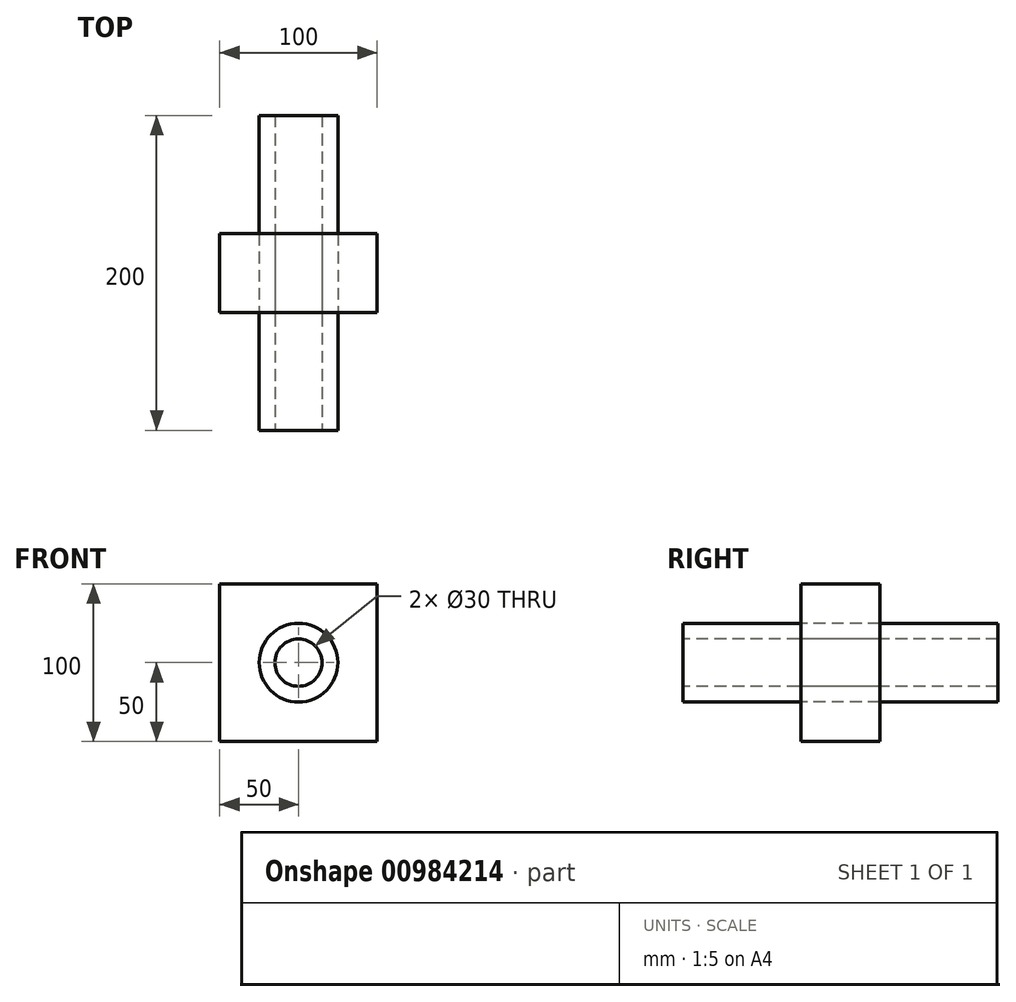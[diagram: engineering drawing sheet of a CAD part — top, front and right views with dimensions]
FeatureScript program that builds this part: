
annotation { "Feature Type Name" : "Feature", "Feature Type Description" : "" }
export const myFeature = defineFeature(function(context is Context, id is Id, definition is map)
    precondition{}
    {
        {
            var Q0;
            Q0=qCreatedBy(makeId("Front.planeOp"),FACE);
            var sketch = newSketch(context, id + "F0", { "sketchPlane" : qUnion([Q0])});
            skLineSegment(sketch, "E0.bottom", {"start": v(50, 50) * mm, "end": v(-50, 50) * mm});
            skLineSegment(sketch, "E0.top", {"start": v(50, -50) * mm, "end": v(-50, -50) * mm});
            skLineSegment(sketch, "E0.left", {"start": v(50, 50) * mm, "end": v(50, -50) * mm});
            skLineSegment(sketch, "E0.right", {"start": v(-50, 50) * mm, "end": v(-50, -50) * mm});
            skPoint(sketch, "E0.middle", {"position": v(0, 0) * mm});
            skSolve(sketch);
        }
        {
            var Q0;
            Q0=makeQuery(id+"F0.imprint","IMPRINT",FACE,{"disambiguationData":[TD([[makeQuery(id+"F0.imprint","IMPRINT",EDGE,{"derivedFrom":sQuery(id+"F0.wireOp",EDGE,"E0.bottom")}),1.0]])]});
            extrude(context, id + "F1", {"entities" : qUnion([Q0]), "oppositeDirection" : true, "depth" : 50 * mm, "offsetDistance" : 25 * mm});
        }
        {
            var Q0;
            Q0=qCreatedBy(makeId("Right.planeOp"),FACE);
            var sketch = newSketch(context, id + "F2", { "sketchPlane" : qUnion([Q0])});
            skLineSegment(sketch, "E1", {"start": v(-91.09, 0) * mm, "end": v(190.65, 0) * mm, "construction": true});
            skLineSegment(sketch, "E2.bottom", {"start": v(-75, 0) * mm, "end": v(125, 0) * mm});
            skLineSegment(sketch, "E2.top", {"start": v(-75, 25) * mm, "end": v(125, 25) * mm});
            skLineSegment(sketch, "E2.left", {"start": v(-75, 0) * mm, "end": v(-75, 25) * mm});
            skLineSegment(sketch, "E2.right", {"start": v(125, 0) * mm, "end": v(125, 25) * mm});
            skPoint(sketch, "E3", {"position": v(0, 0) * mm});
            skSolve(sketch);
        }
        {
            var Q0;
            Q0=makeQuery(id+"F2.imprint","IMPRINT",FACE,{"disambiguationData":[TD([[makeQuery(id+"F2.imprint","IMPRINT",EDGE,{"derivedFrom":sQuery(id+"F2.wireOp",EDGE,"E2.bottom")}),1.0]])]});
            var Q1;
            Q1=sQuery(id+"F2.wireOp",EDGE,"E1");
            revolve(context, id + "F3", {"surfaceOperationType" : NewSurfaceOperationType.NEW, "entities" : qUnion([Q0]), "axis" : qUnion([Q1]), "revolveType" : RevolveType.FULL});
        }
        {
            var Q0;
            Q0=makeQuery(id+"F3.opRevolve","SWEPT_FACE",FACE,{"disambiguationData":[OSD([sQuery(id+"F2.wireOp",EDGE,"E2.left")])]});
            var sketch = newSketch(context, id + "F4", { "sketchPlane" : qUnion([Q0])});
            skPoint(sketch, "E4", {"position": v(0, 0) * mm});
            skSolve(sketch);
        }
        {
            var Q0;
            Q0=sQuery(id+"F4.wireOp",VERTEX,"E4");
            var Q1;
            Q1=makeQuery(id+"F1.opExtrude","SWEPT_BODY",BODY,{"disambiguationData":[OSD([sQuery(id+"F0.wireOp",EDGE,"E0.bottom"),sQuery(id+"F0.wireOp",EDGE,"E0.top"),sQuery(id+"F0.wireOp",EDGE,"E0.left"),sQuery(id+"F0.wireOp",EDGE,"E0.right")])]});
            var Q2;
            Q2=makeQuery(id+"F3.opRevolve","SWEPT_BODY",BODY,{"disambiguationData":[OSD([sQuery(id+"F2.wireOp",EDGE,"E2.bottom"),sQuery(id+"F2.wireOp",EDGE,"E2.top"),sQuery(id+"F2.wireOp",EDGE,"E2.left"),sQuery(id+"F2.wireOp",EDGE,"E2.right")])]});
            hole(context, id + "F5", {"style" : HoleStyle.SIMPLE, "endStyle" : HoleEndStyle.THROUGH, "holeDiameter" : 30 * mm, "majorDiameter" : 5 * mm, "isTappedThrough" : true, "tappedDepth" : 12 * mm, "tapClearance" : 3, "locations" : qUnion([Q0]), "scope" : qUnion([Q1, Q2])});
        }
    });
